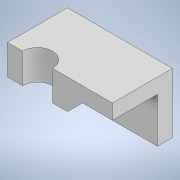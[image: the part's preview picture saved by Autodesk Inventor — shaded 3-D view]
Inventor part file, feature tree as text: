
AUTODESK INVENTOR PART (.ipt)
format: ipt  version: 2020 (Build 240168000, 168)  size: 139,776 bytes
history: native  units: mm
features: sketch x4, extrude x3, other x1, loft x1
ambient origin geometry x8: Origin, YZ Plane, XZ Plane, XY Plane, X Axis, Y Axis, Z Axis, Center Point
bodies: Body1 (feature_tree)
feature tree (9):
  other  "實體1"
  extrude  "擠出1"  Depth=70.0mm
  extrude  "擠出2"  Depth=40.0mm
  extrude  "擠出3"  Depth=10.0mm TaperAngle=0.0deg
  sketch  "草圖4"
  loft  "斷面混成2"
  sketch  "草圖1"
  sketch  "草圖2"
  sketch  "草圖3"
